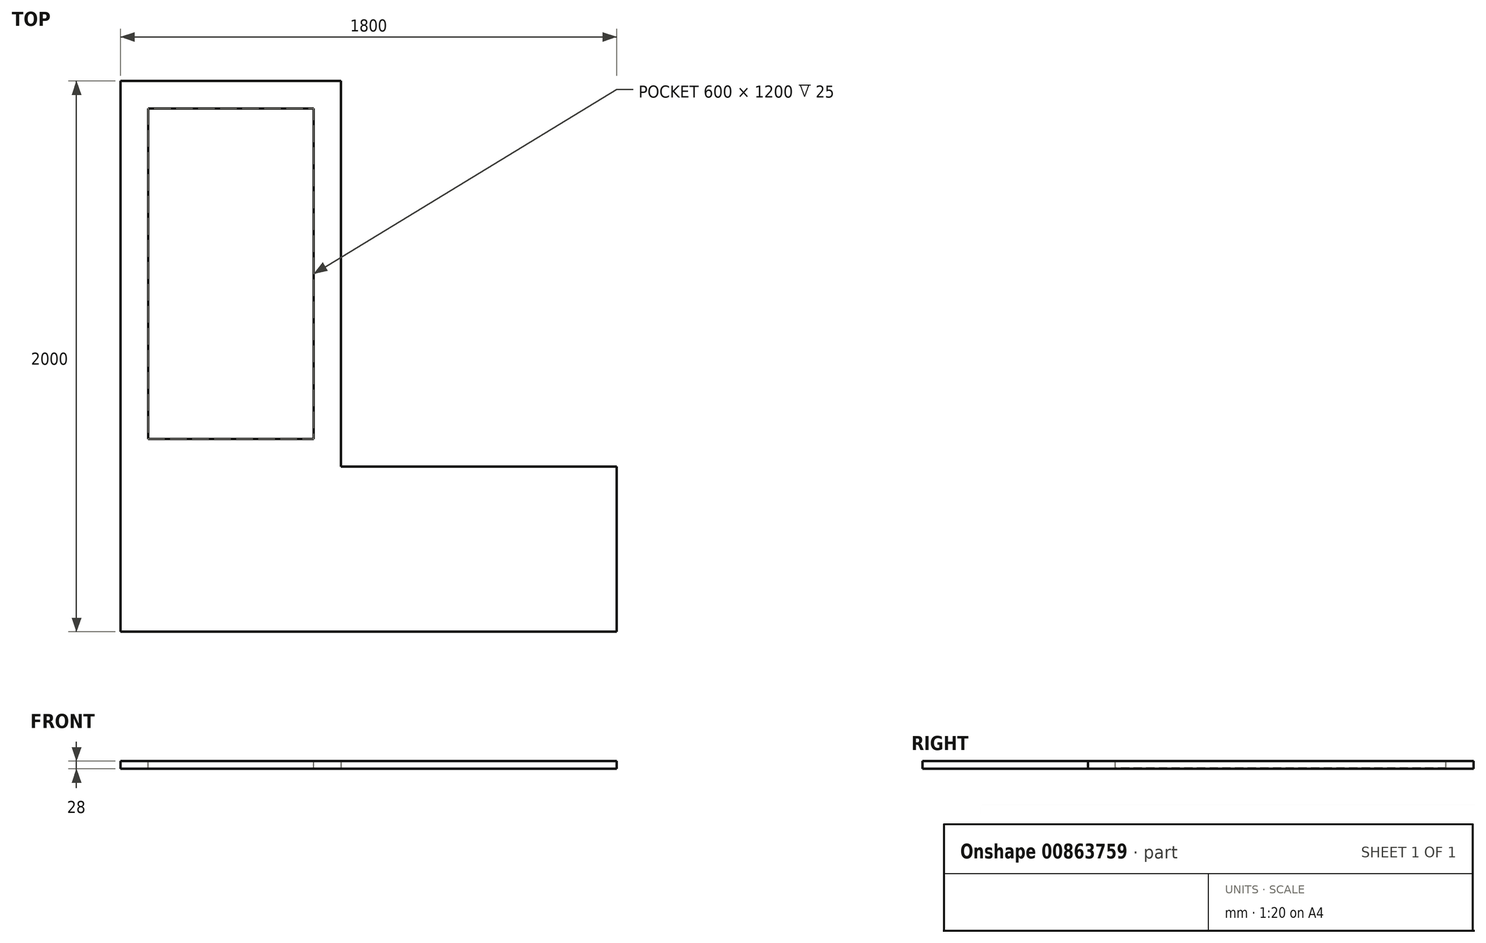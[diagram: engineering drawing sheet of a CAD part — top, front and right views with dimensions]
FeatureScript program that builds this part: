
annotation { "Feature Type Name" : "Feature", "Feature Type Description" : "" }
export const myFeature = defineFeature(function(context is Context, id is Id, definition is map)
    precondition{}
    {
        {
            var Q0;
            Q0=qCreatedBy(makeId("Top.planeOp"),FACE);
            var sketch = newSketch(context, id + "F0", { "sketchPlane" : qUnion([Q0])});
            skLineSegment(sketch, "E0", {"start": v(0, 0) * mm, "end": v(0, 2000) * mm});
            skLineSegment(sketch, "E1", {"start": v(0, 2000) * mm, "end": v(800, 2000) * mm});
            skLineSegment(sketch, "E2", {"start": v(800, 2000) * mm, "end": v(800, 600) * mm});
            skLineSegment(sketch, "E3", {"start": v(800, 600) * mm, "end": v(1800, 600) * mm});
            skLineSegment(sketch, "E4", {"start": v(1800, 600) * mm, "end": v(1800, 0) * mm});
            skLineSegment(sketch, "E5", {"start": v(1800, 0) * mm, "end": v(0, 0) * mm});
            skSolve(sketch);
        }
        {
            var Q0;
            Q0=makeQuery(id+"F0.imprint","IMPRINT",FACE,{"disambiguationData":[TD([[makeQuery(id+"F0.imprint","IMPRINT",EDGE,{"derivedFrom":sQuery(id+"F0.wireOp",EDGE,"E0")}),-1.0]])]});
            extrude(context, id + "F1", {"entities" : qUnion([Q0]), "depth" : 28 * mm, "offsetDistance" : 25 * mm});
        }
        {
            var Q0;
            Q0=makeQuery(id+"F1.opExtrude","CAP_FACE",FACE,{"disambiguationData":[OSD([sQuery(id+"F0.wireOp",EDGE,"E0"),sQuery(id+"F0.wireOp",EDGE,"E1"),sQuery(id+"F0.wireOp",EDGE,"E2"),sQuery(id+"F0.wireOp",EDGE,"E3"),sQuery(id+"F0.wireOp",EDGE,"E4"),sQuery(id+"F0.wireOp",EDGE,"E5")])],"isStart":false});
            var sketch = newSketch(context, id + "F2", { "sketchPlane" : qUnion([Q0])});
            skLineSegment(sketch, "E6", {"start": v(400, 2000) * mm, "end": v(400, 0) * mm, "construction": true});
            skLineSegment(sketch, "E7", {"start": v(1800, 300) * mm, "end": v(0, 300) * mm, "construction": true});
            skLineSegment(sketch, "E8.bottom", {"start": v(100, 1900) * mm, "end": v(700, 1900) * mm});
            skLineSegment(sketch, "E8.top", {"start": v(100, 700) * mm, "end": v(700, 700) * mm});
            skLineSegment(sketch, "E8.left", {"start": v(100, 1900) * mm, "end": v(100, 700) * mm});
            skLineSegment(sketch, "E8.right", {"start": v(700, 1900) * mm, "end": v(700, 700) * mm});
            skPoint(sketch, "E8.middle", {"position": v(400, 1300) * mm});
            skSolve(sketch);
        }
        {
            var Q0;
            Q0=makeQuery(id+"F2.imprint","IMPRINT",FACE,{"disambiguationData":[TD([[makeQuery(id+"F2.imprint","IMPRINT",EDGE,{"derivedFrom":sQuery(id+"F2.wireOp",EDGE,"E8.bottom")}),-1.0]])]});
            extrude(context, id + "F3", {"entities" : qUnion([Q0]), "operationType" : NewBodyOperationType.REMOVE, "oppositeDirection" : true, "depth" : 25 * mm, "offsetDistance" : 25 * mm});
        }
        {
            var Q0;
            Q0=makeQuery(id+"F1.opExtrude","CAP_FACE",FACE,{"disambiguationData":[OSD([sQuery(id+"F0.wireOp",EDGE,"E0"),sQuery(id+"F0.wireOp",EDGE,"E1"),sQuery(id+"F0.wireOp",EDGE,"E2"),sQuery(id+"F0.wireOp",EDGE,"E3"),sQuery(id+"F0.wireOp",EDGE,"E4"),sQuery(id+"F0.wireOp",EDGE,"E5")])],"isStart":true});
            var sketch = newSketch(context, id + "F4", { "sketchPlane" : qUnion([Q0])});
            skLineSegment(sketch, "E9", {"start": v(0, -150) * mm, "end": v(1800, -150) * mm, "construction": true});
            skLineSegment(sketch, "E10", {"start": v(0, -450) * mm, "end": v(1800, -450) * mm, "construction": true});
            skLineSegment(sketch, "E11", {"start": v(150, 0) * mm, "end": v(150, -2000) * mm, "construction": true});
            skLineSegment(sketch, "E12", {"start": v(650, 0) * mm, "end": v(650, -2000) * mm, "construction": true});
            skLineSegment(sketch, "E13", {"start": v(1650, 0) * mm, "end": v(1650, -600) * mm, "construction": true});
            skLineSegment(sketch, "E14", {"start": v(0, -1850) * mm, "end": v(800, -1850) * mm, "construction": true});
            skCircle(sketch, "E15", {"center": v(150, -150) * mm, "radius": 40 * mm});
            skCircle(sketch, "E16", {"center": v(1650, -150) * mm, "radius": 40 * mm});
            skCircle(sketch, "E17", {"center": v(1650, -450) * mm, "radius": 40 * mm});
            skCircle(sketch, "E18", {"center": v(650, -1850) * mm, "radius": 40 * mm});
            skCircle(sketch, "E19", {"center": v(150, -1850) * mm, "radius": 40 * mm});
            skLineSegment(sketch, "E20", {"start": v(0, 0) * mm, "end": v(800, -600) * mm, "construction": true});
            skLineSegment(sketch, "E21", {"start": v(800, -600) * mm, "end": v(0, -600) * mm, "construction": true});
            skCircle(sketch, "E22", {"center": v(150, -600) * mm, "radius": 40 * mm});
            skSolve(sketch);
        }
        {
            var Q0;
            Q0=sQuery(id+"F4.wireOp",EDGE,"E15");
            extrude(context, id + "F5", {"bodyType" : ToolBodyType.SURFACE, "surfaceEntities" : qUnion([Q0]), "depth" : 750 * mm, "offsetDistance" : 25 * mm});
        }
        {
            var Q0;
            Q0=sQuery(id+"F4.wireOp",EDGE,"E16");
            var Q1;
            Q1=sQuery(id+"F4.wireOp",EDGE,"cASUG08o-81MH-8D0S-e8uf-AotksKHfqTZH");
            extrude(context, id + "F6", {"bodyType" : ToolBodyType.SURFACE, "surfaceEntities" : qUnion([Q0, Q1]), "depth" : 750 * mm, "offsetDistance" : 25 * mm});
        }
        {
            var Q0;
            Q0=sQuery(id+"F4.wireOp",EDGE,"E19");
            var Q1;
            Q1=sQuery(id+"F4.wireOp",EDGE,"E18");
            extrude(context, id + "F7", {"bodyType" : ToolBodyType.SURFACE, "surfaceEntities" : qUnion([Q0, Q1]), "depth" : 750 * mm, "offsetDistance" : 25 * mm});
        }
        {
            var Q0;
            Q0=sQuery(id+"F4.wireOp",EDGE,"E17");
            var Q1;
            Q1=sQuery(id+"F4.wireOp",EDGE,"tMBmCi8t-LLYb-dIf8-yHKL-t8eQV2Jex4m3");
            var Q2;
            Q2=sQuery(id+"F4.wireOp",EDGE,"cPQXWBMX-fk51-AnHo-0bC0-mN9ykz6zl7Ki");
            extrude(context, id + "F8", {"bodyType" : ToolBodyType.SURFACE, "surfaceEntities" : qUnion([Q0, Q1, Q2]), "depth" : 750 * mm, "offsetDistance" : 25 * mm});
        }
    });
